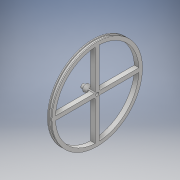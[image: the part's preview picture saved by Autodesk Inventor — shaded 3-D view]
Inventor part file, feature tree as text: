
AUTODESK INVENTOR PART (.ipt)
format: ipt  version: 2018 (Build 220112000, 112)  size: 205,824 bytes
history: native  units: mm
features: extrude x12, sketch x12, pattern_circular x1, fillet x1
ambient origin geometry x8: Origin, YZ Plane, XZ Plane, XY Plane, X Axis, Y Axis, Z Axis, Center Point
bodies: Solid1 (feature_tree)
feature tree (26):
  extrude  "Extrusion1"  Depth=3.5mm TaperAngle=0.0deg
  extrude  "Extrusion2"  Depth=1.0mm TaperAngle=0.0deg
  extrude  "Extrusion3"  Depth=1.0mm TaperAngle=0.0deg
  extrude  "Extrusion4"  Depth=6.0mm TaperAngle=0.0deg
  extrude  "Extrusion5"  Depth=10.0mm TaperAngle=0.0deg
  extrude  "Extrusion6"  Depth=1.0mm TaperAngle=0.0deg
  extrude  "Extrusion7"  Depth=1.0mm
  extrude  "Extrusion8"  Depth=10.0mm
  extrude  "Extrusion9"  Depth=40.0mm TaperAngle=360.0deg
  extrude  "Extrusion10"  Depth=2.0mm TaperAngle=0.0deg
  pattern_circular  "Circular Pattern1"  [2 undecoded]
  fillet  "Fillet1"  [1 undecoded]
  extrude  "Extrusion11"  [1 undecoded]
  extrude  "Extrusion12"  [1 undecoded]
  sketch  "Sketch1"  dims[d0=88.0mm d1=3.5mm d2=0.0mm]
  sketch  "Sketch2"  dims[d3=90.0mm d4=1.0mm d5=0.0mm]
  sketch  "Sketch3"  dims[d6=90.0mm d7=1.0mm d8=0.0mm]
  sketch  "Sketch4"  dims[d9=83.0mm d10=6.0mm d11=0.0mm]
  sketch  "Sketch5"  dims[d12=7.0mm d13=10.0mm d14=0.0mm]
  sketch  "Sketch6"  dims[d15=2.0mm d16=0.0mm d17=1.0mm d18=0.0mm]
  sketch  "Sketch7"  dims[d19=1.0mm d20=0.0mm d21=3.25mm]
  sketch  "Sketch8"  dims[d22=10.0mm d23=0.0mm d24=4.0mm]
  sketch  "Sketch9"  dims[d25=4.5mm d26=0.0mm d27=40.0mm d28=360.0deg]
  sketch  "Sketch10"  dims[d30=2.0mm d31=2.0mm d32=0.0mm]
  sketch  "Sketch11"  dims[d33=4.0mm]
  sketch  "Sketch12"  dims[d34=3.3mm d35=0.0mm]
note: 5 required parameter values undecoded (feature->parameter linkage not recoverable at this tier; creation-order binding heuristic only, values carry confidence <= 0.55)
